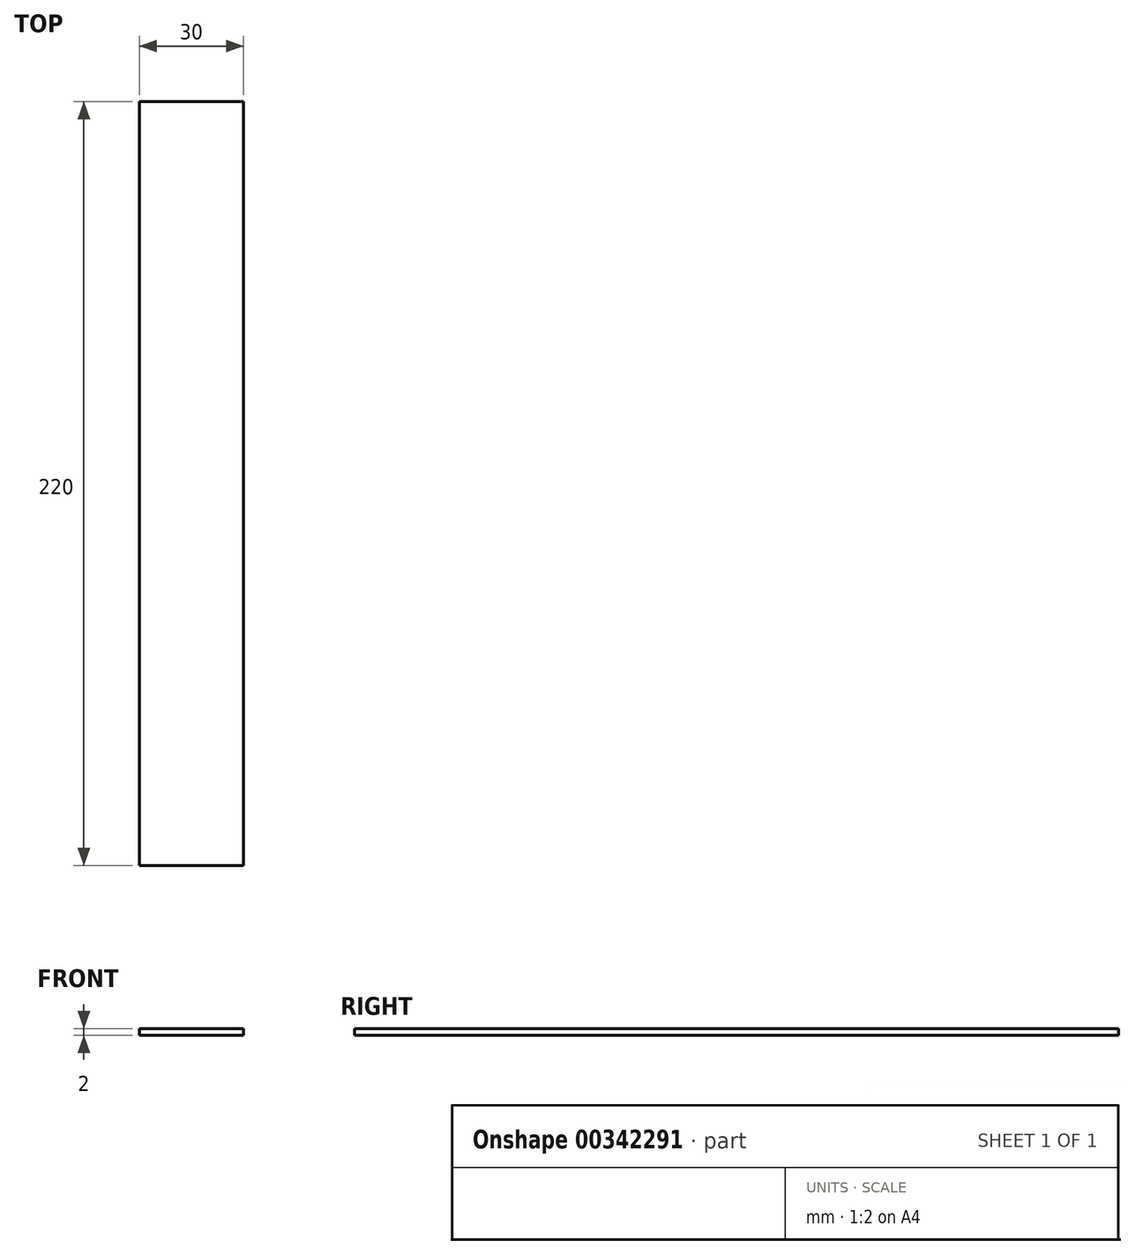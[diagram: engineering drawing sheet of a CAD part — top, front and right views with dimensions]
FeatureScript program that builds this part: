
annotation { "Feature Type Name" : "Feature", "Feature Type Description" : "" }
export const myFeature = defineFeature(function(context is Context, id is Id, definition is map)
    precondition{}
    {
        {
            var Q0;
            Q0=qCreatedBy(makeId("Top.planeOp"),FACE);
            var sketch = newSketch(context, id + "F0", { "sketchPlane" : qUnion([Q0])});
            skLineSegment(sketch, "E0.bottom", {"start": v(0, 0) * mm, "end": v(-30, 0) * mm});
            skLineSegment(sketch, "E0.top", {"start": v(0, 220) * mm, "end": v(-30, 220) * mm});
            skLineSegment(sketch, "E0.left", {"start": v(0, 0) * mm, "end": v(0, 220) * mm});
            skLineSegment(sketch, "E0.right", {"start": v(-30, 0) * mm, "end": v(-30, 220) * mm});
            skSolve(sketch);
        }
        {
            var Q0;
            Q0=makeQuery(id+"F0.imprint","IMPRINT",FACE,{"disambiguationData":[TD([[makeQuery(id+"F0.imprint","IMPRINT",EDGE,{"derivedFrom":sQuery(id+"F0.wireOp",EDGE,"E0.bottom")}),-1.0]])]});
            extrude(context, id + "F1", {"entities" : qUnion([Q0]), "depth" : 2 * mm});
        }
    });
